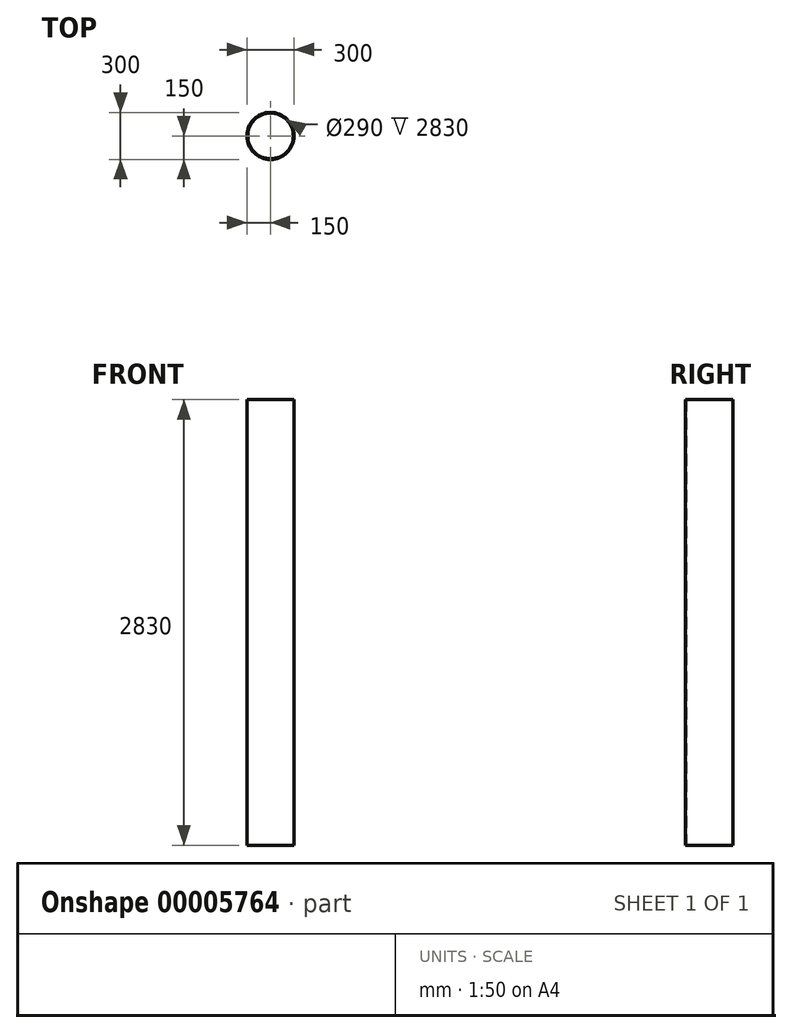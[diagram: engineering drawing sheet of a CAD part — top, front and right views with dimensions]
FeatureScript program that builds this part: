
annotation { "Feature Type Name" : "Feature", "Feature Type Description" : "" }
export const myFeature = defineFeature(function(context is Context, id is Id, definition is map)
    precondition{}
    {
        {
            var Q0;
            Q0=qCreatedBy(makeId("Top.planeOp"),FACE);
            var sketch = newSketch(context, id + "F0", { "sketchPlane" : qUnion([Q0])});
            skCircle(sketch, "E0", {"center": v(0, 0) * mm, "radius": 150 * mm});
            skCircle(sketch, "E1", {"center": v(0, 0) * mm, "radius": 145 * mm});
            skSolve(sketch);
        }
        {
            var Q0;
            Q0=makeQuery(id+"F0.imprint","IMPRINT",FACE,{"disambiguationData":[TD([[makeQuery(id+"F0.imprint","IMPRINT",EDGE,{"derivedFrom":sQuery(id+"F0.wireOp",EDGE,"E0")}),1.0]])]});
            extrude(context, id + "F1", {"entities" : qUnion([Q0]), "depth" : 2830 * mm});
        }
    });
